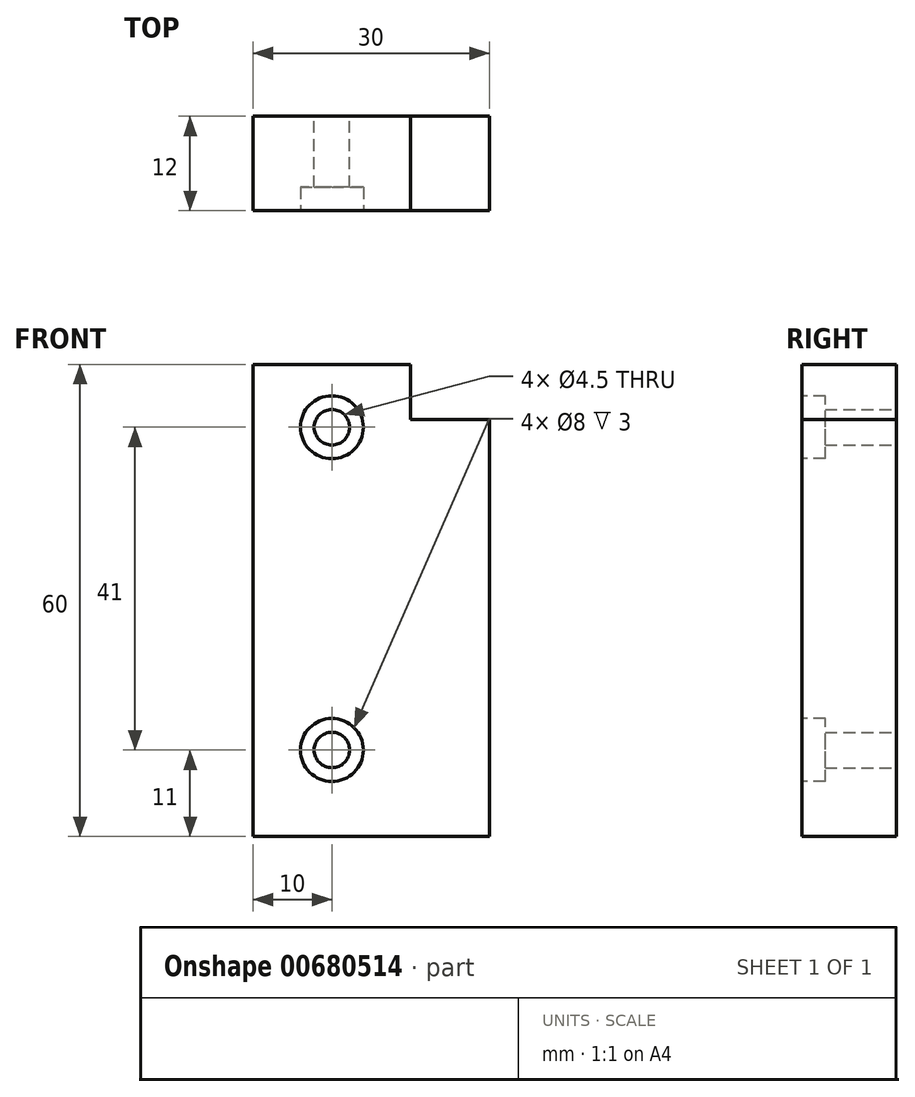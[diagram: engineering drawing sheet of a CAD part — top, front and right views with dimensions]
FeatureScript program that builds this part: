
annotation { "Feature Type Name" : "Feature", "Feature Type Description" : "" }
export const myFeature = defineFeature(function(context is Context, id is Id, definition is map)
    precondition{}
    {
        {
            var Q0;
            Q0=qCreatedBy(makeId("Front.planeOp"),FACE);
            var sketch = newSketch(context, id + "F0", { "sketchPlane" : qUnion([Q0])});
            skLineSegment(sketch, "E0.bottom", {"start": v(0, 0) * mm, "end": v(30, 0) * mm});
            skLineSegment(sketch, "E0.top", {"start": v(0, 60) * mm, "end": v(30, 60) * mm});
            skLineSegment(sketch, "E0.left", {"start": v(0, 0) * mm, "end": v(0, 60) * mm});
            skLineSegment(sketch, "E0.right", {"start": v(30, 0) * mm, "end": v(30, 60) * mm});
            skCircle(sketch, "E1", {"center": v(10, 52) * mm, "radius": 2.25 * mm});
            skCircle(sketch, "E2", {"center": v(10, 11) * mm, "radius": 2.25 * mm});
            skLineSegment(sketch, "E3.bottom", {"start": v(30, 60) * mm, "end": v(20, 60) * mm});
            skLineSegment(sketch, "E3.top", {"start": v(30, 53) * mm, "end": v(20, 53) * mm});
            skLineSegment(sketch, "E3.left", {"start": v(30, 60) * mm, "end": v(30, 53) * mm});
            skLineSegment(sketch, "E3.right", {"start": v(20, 60) * mm, "end": v(20, 53) * mm});
            skSolve(sketch);
        }
        {
            var Q0;
            Q0=makeQuery(id+"F0.imprint","IMPRINT",FACE,{"disambiguationData":[TD([[makeQuery(id+"F0.imprint","IMPRINT",EDGE,{"derivedFrom":sQuery(id+"F0.wireOp",EDGE,"E0.bottom")}),1.0]])]});
            extrude(context, id + "F1", {"entities" : qUnion([Q0]), "depth" : 12 * mm, "offsetDistance" : 25 * mm});
        }
        {
            var Q0;
            Q0=makeQuery(id+"F1.opExtrude","CAP_FACE",FACE,{"disambiguationData":[OSD([sQuery(id+"F0.wireOp",EDGE,"E0.bottom"),sQuery(id+"F0.wireOp",EDGE,"E0.top"),sQuery(id+"F0.wireOp",EDGE,"E0.left"),sQuery(id+"F0.wireOp",EDGE,"E0.right"),sQuery(id+"F0.wireOp",EDGE,"E1"),sQuery(id+"F0.wireOp",EDGE,"E2")])],"isStart":false});
            var sketch = newSketch(context, id + "F2", { "sketchPlane" : qUnion([Q0])});
            skCircle(sketch, "E4", {"center": v(10, 52) * mm, "radius": 4 * mm});
            skCircle(sketch, "E5", {"center": v(10, 11) * mm, "radius": 4 * mm});
            skSolve(sketch);
        }
        {
            var Q0;
            Q0=makeQuery(id+"F2.imprint","IMPRINT",FACE,{"disambiguationData":[TD([[makeQuery(id+"F2.imprint","IMPRINT",EDGE,{"derivedFrom":sQuery(id+"F2.wireOp",EDGE,"E4")}),1.0]])]});
            var Q1;
            Q1=makeQuery(id+"F2.imprint","IMPRINT",FACE,{"disambiguationData":[TD([[makeQuery(id+"F2.imprint","IMPRINT",EDGE,{"derivedFrom":sQuery(id+"F2.wireOp",EDGE,"E5")}),1.0]])]});
            extrude(context, id + "F3", {"entities" : qUnion([Q0, Q1]), "operationType" : NewBodyOperationType.REMOVE, "oppositeDirection" : true, "depth" : 3 * mm, "offsetDistance" : 25 * mm});
        }
    });
